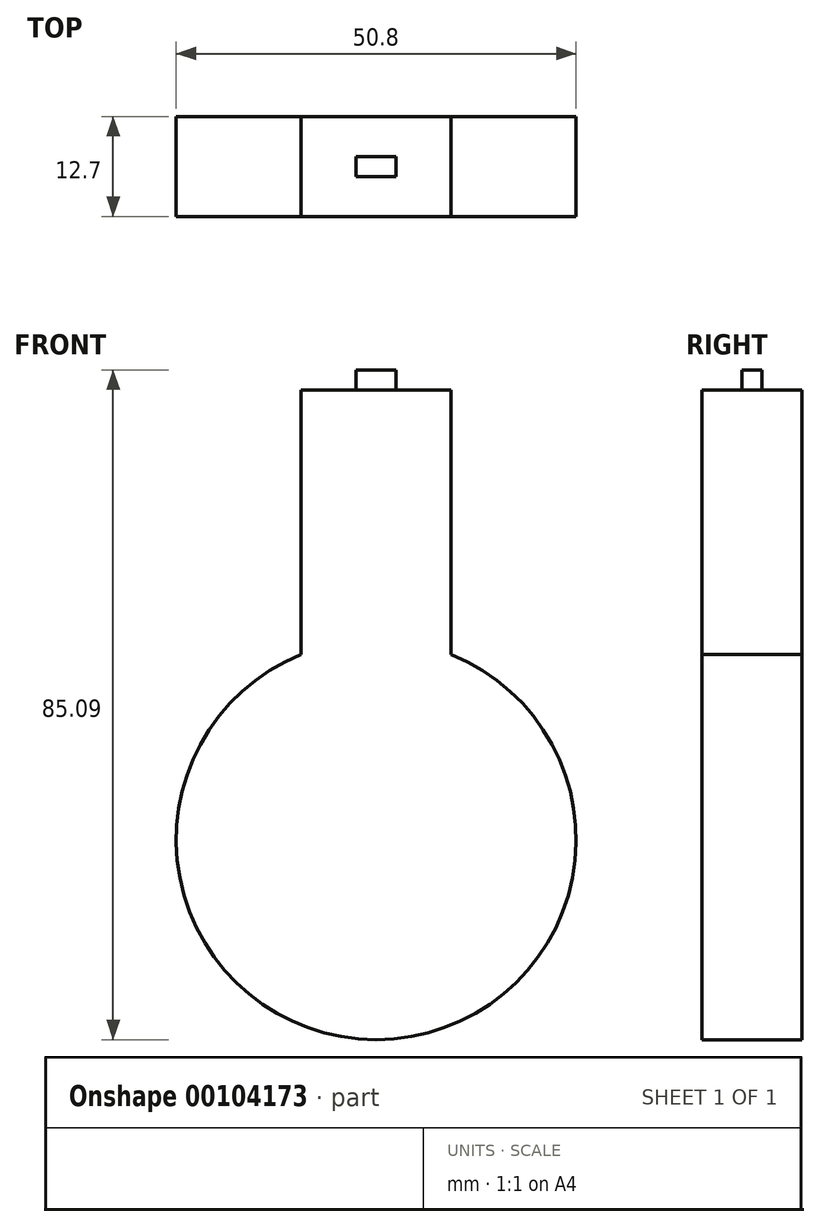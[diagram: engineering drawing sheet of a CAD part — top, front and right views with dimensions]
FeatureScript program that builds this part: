
annotation { "Feature Type Name" : "Feature", "Feature Type Description" : "" }
export const myFeature = defineFeature(function(context is Context, id is Id, definition is map)
    precondition{}
    {
        {
            var Q0;
            Q0=qCreatedBy(makeId("Front.planeOp"),FACE);
            var sketch = newSketch(context, id + "F3", { "sketchPlane" : qUnion([Q0])});
            skLineSegment(sketch, "E0.bottom", {"start": v(-50.41, 69.24) * mm, "end": v(-31.36, 69.24) * mm});
            skLineSegment(sketch, "E0.top", {"start": v(-50.41, 12.09) * mm, "end": v(-31.36, 12.09) * mm});
            skLineSegment(sketch, "E0.left", {"start": v(-50.41, 69.24) * mm, "end": v(-50.41, 12.09) * mm});
            skLineSegment(sketch, "E0.right", {"start": v(-31.36, 69.24) * mm, "end": v(-31.36, 12.09) * mm});
            skPoint(sketch, "E1", {"position": v(-40.89, 12.09) * mm});
            skCircle(sketch, "E2", {"center": v(-40.89, 12.09) * mm, "radius": 25.4 * mm});
            skSolve(sketch);
        }
        {
            var Q0;
            {var subQ0=sQuery(id+"F3.wireOp",EDGE,"E0.bottom");Q0=makeQuery(id+"F3.imprint","IMPRINT",FACE,{"disambiguationData":[TD([[makeQuery(id+"F3.imprint","IMPRINT",EDGE,{"derivedFrom":subQ0}),-1.0]])]});}
            var Q1;
            {var subQ0=sQuery(id+"F3.wireOp",EDGE,"E0.top");Q1=makeQuery(id+"F3.imprint","IMPRINT",FACE,{"disambiguationData":[TD([[makeQuery(id+"F3.imprint","IMPRINT",EDGE,{"derivedFrom":subQ0}),1.0]])]});}
            var Q2;
            {var subQ0=sQuery(id+"F3.wireOp",EDGE,"E0.top");Q2=makeQuery(id+"F3.imprint","IMPRINT",FACE,{"disambiguationData":[TD([[makeQuery(id+"F3.imprint","IMPRINT",EDGE,{"derivedFrom":subQ0}),-1.0]])]});}
            extrude(context, id + "F0", {"entities" : qUnion([Q0, Q1, Q2]), "depth" : 12.7 * mm});
        }
        {
            var Q0;
            Q0=makeQuery(id+"F0.opExtrude","SWEPT_FACE",FACE,{"disambiguationData":[OSD([sQuery(id+"F3.wireOp",EDGE,"E0.bottom")])]});
            var sketch = newSketch(context, id + "F1", { "sketchPlane" : qUnion([Q0])});
            skLineSegment(sketch, "E3.bottom", {"start": v(-43.43, -5.08) * mm, "end": v(-38.35, -5.08) * mm});
            skLineSegment(sketch, "E3.top", {"start": v(-43.43, -7.62) * mm, "end": v(-38.35, -7.62) * mm});
            skLineSegment(sketch, "E3.left", {"start": v(-43.43, -5.08) * mm, "end": v(-43.43, -7.62) * mm});
            skLineSegment(sketch, "E3.right", {"start": v(-38.35, -5.08) * mm, "end": v(-38.35, -7.62) * mm});
            skSolve(sketch);
        }
        {
            var Q0;
            Q0=makeQuery(id+"F1.imprint","IMPRINT",FACE,{"disambiguationData":[TD([[makeQuery(id+"F1.imprint","IMPRINT",EDGE,{"derivedFrom":sQuery(id+"F1.wireOp",EDGE,"E3.bottom")}),-1.0]])]});
            extrude(context, id + "F2", {"entities" : qUnion([Q0]), "operationType" : NewBodyOperationType.ADD, "depth" : 2.54 * mm});
        }
    });
